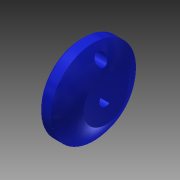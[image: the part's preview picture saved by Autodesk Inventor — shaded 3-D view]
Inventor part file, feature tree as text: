
AUTODESK INVENTOR PART (.ipt)
format: ipt  version: 2014 (Build 180170000, 170)  size: 155,648 bytes
history: native  units: in
note: dims shown in document units (in); Inventor stores cm internally (conversion verified against a paired STEP export)
features: sketch x5, extrude x4, plane x2, revolve x1, chamfer x1, reference x1
ambient origin geometry x8: Origin, YZ Plane, XZ Plane, XY Plane, X Axis, Y Axis, Z Axis, Center Point
bodies: Solid1 (feature_tree)
feature tree (14):
  revolve  "Revolution1"  [1 undecoded]
  plane  "Work Plane3"
  extrude  "Extrusion1"  Depth=0.127in
  extrude  "Extrusion2"  Depth=0.2725in
  extrude  "Extrusion3"  TaperAngle=90.0deg  [1 undecoded]
  chamfer  "Chamfer1"  Distance=0.125in
  extrude  "Extrusion4"  Depth=0.26in TaperAngle=0.0deg
  sketch  "Sketch1"  dims[d0=0.08in d1=0.5315in]
  plane  "Work Plane2"
  sketch  "Sketch2"  dims[d2=0.24in d3=0.127in]
  sketch  "Sketch3"  dims[d4=0.15in d5=0.2725in]
  sketch  "Sketch4"  dims[d7=0.2in d8=90.0deg]
  reference  "Reference1"
  sketch  "Sketch5"  dims[d9=-0.05in d10=0.125in d11=0.26in d12=0.0in d13=0.09in d14=0.26in d15=0.0in d16=0.26in d17=0.0in d18=0.03in d19=0.125in d20=45.0deg d21=1.0in d22=0.0in]
note: 2 required parameter values undecoded (feature->parameter linkage not recoverable at this tier; creation-order binding heuristic only, values carry confidence <= 0.55)